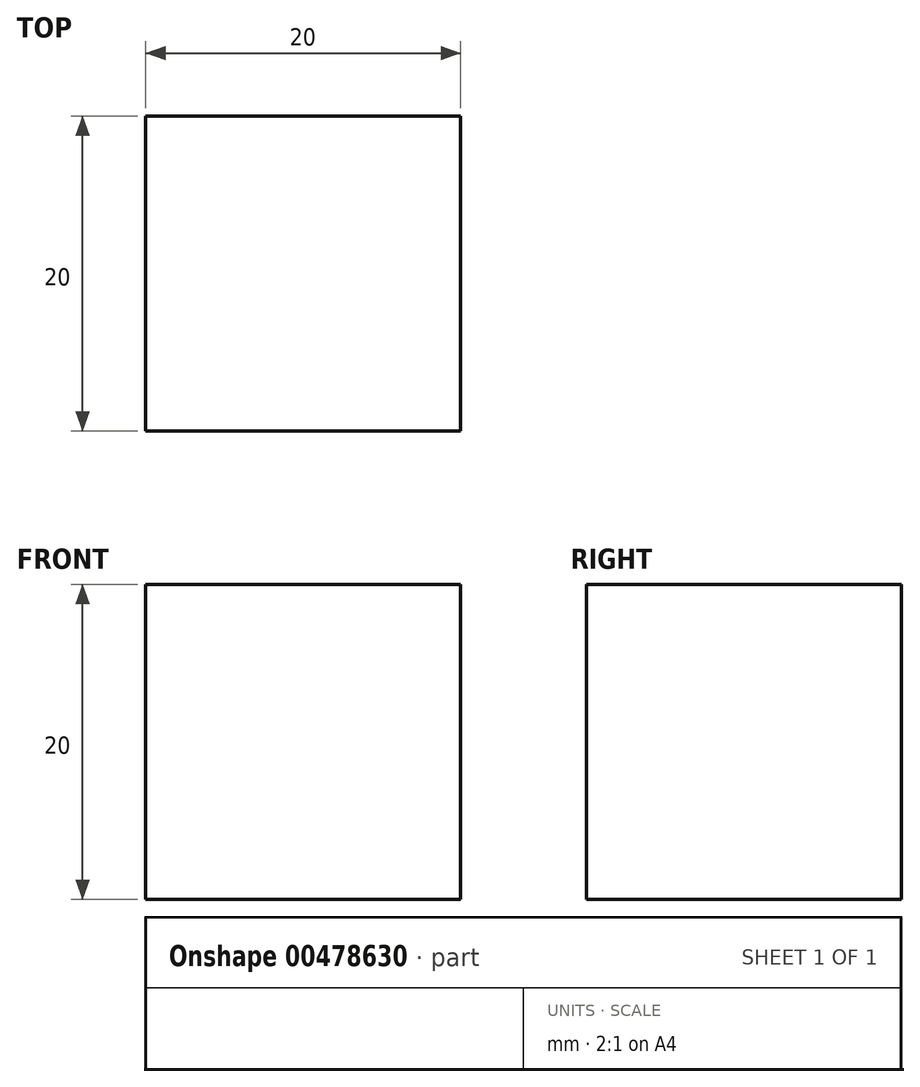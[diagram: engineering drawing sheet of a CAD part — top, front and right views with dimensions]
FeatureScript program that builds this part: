
annotation { "Feature Type Name" : "Feature", "Feature Type Description" : "" }
export const myFeature = defineFeature(function(context is Context, id is Id, definition is map)
    precondition{}
    {
        {
            var Q0;
            Q0=qCreatedBy(makeId("Top.planeOp"),FACE);
            var sketch = newSketch(context, id + "F0", { "sketchPlane" : qUnion([Q0])});
            skLineSegment(sketch, "E0.bottom", {"start": v(-17.05, 10.4) * mm, "end": v(2.95, 10.4) * mm});
            skLineSegment(sketch, "E0.top", {"start": v(-17.05, -9.6) * mm, "end": v(2.95, -9.6) * mm});
            skLineSegment(sketch, "E0.left", {"start": v(-17.05, 10.4) * mm, "end": v(-17.05, -9.6) * mm});
            skLineSegment(sketch, "E0.right", {"start": v(2.95, 10.4) * mm, "end": v(2.95, -9.6) * mm});
            skSolve(sketch);
        }
        {
            var Q0;
            Q0 = qSketchRegion(id + "F0", true);
            extrude(context, id + "F1", {"entities" : qUnion([Q0]), "depth" : 20 * mm});
        }
    });
